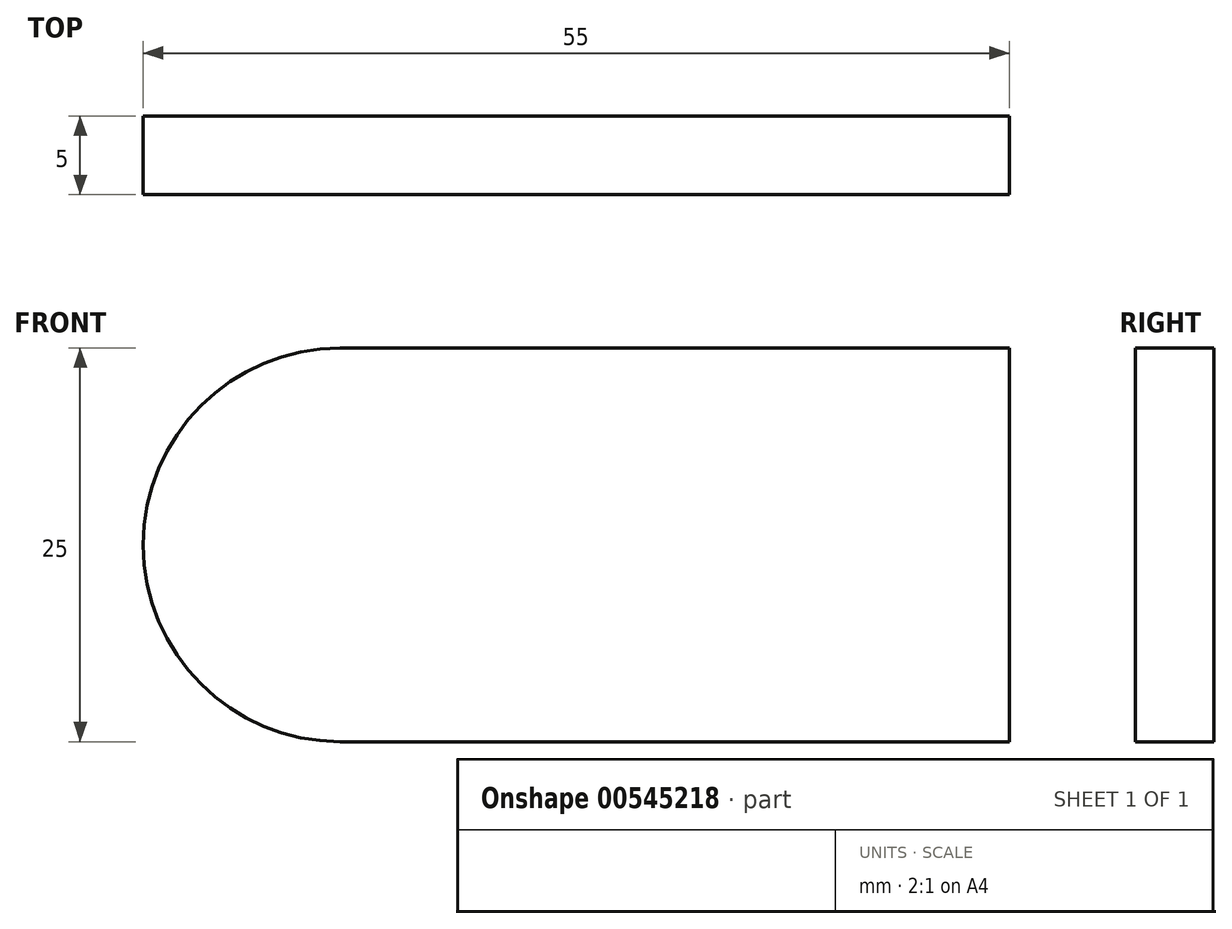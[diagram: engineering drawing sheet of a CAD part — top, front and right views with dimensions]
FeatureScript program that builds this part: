
annotation { "Feature Type Name" : "Feature", "Feature Type Description" : "" }
export const myFeature = defineFeature(function(context is Context, id is Id, definition is map)
    precondition{}
    {
        {
            var Q0;
            Q0=qCreatedBy(makeId("Front.planeOp"),FACE);
            var sketch = newSketch(context, id + "F0", { "sketchPlane" : qUnion([Q0])});
            skLineSegment(sketch, "E0.bottom", {"start": v(-42.5, 0) * mm, "end": v(0, 0) * mm});
            skLineSegment(sketch, "E0.top", {"start": v(-42.5, -25) * mm, "end": v(0, -25) * mm});
            skLineSegment(sketch, "E0.left", {"start": v(-55, -12.5) * mm, "end": v(-55, -12.5) * mm});
            skLineSegment(sketch, "E0.right", {"start": v(0, 0) * mm, "end": v(0, -25) * mm});
            skPoint(sketch, "E1.visualSharp", {"position": v(-55, -25) * mm});
            skArc(sketch, "E1.filletArc", {"start": v(-55, -12.5) * mm, "mid": v(-51.34, -21.34) * mm, "end": v(-42.5, -25) * mm});
            skPoint(sketch, "E2.visualSharp", {"position": v(-55, 0) * mm});
            skArc(sketch, "E2.filletArc", {"start": v(-42.5, 0) * mm, "mid": v(-51.34, -3.66) * mm, "end": v(-55, -12.5) * mm});
            skSolve(sketch);
        }
        {
            var Q0;
            Q0=makeQuery(id+"F0.imprint","IMPRINT",FACE,{"disambiguationData":[TD([[makeQuery(id+"F0.imprint","IMPRINT",EDGE,{"derivedFrom":sQuery(id+"F0.wireOp",EDGE,"E0.bottom")}),-1.0]])]});
            extrude(context, id + "F1", {"entities" : qUnion([Q0]), "depth" : 5 * mm, "offsetDistance" : 25.4 * mm});
        }
    });
